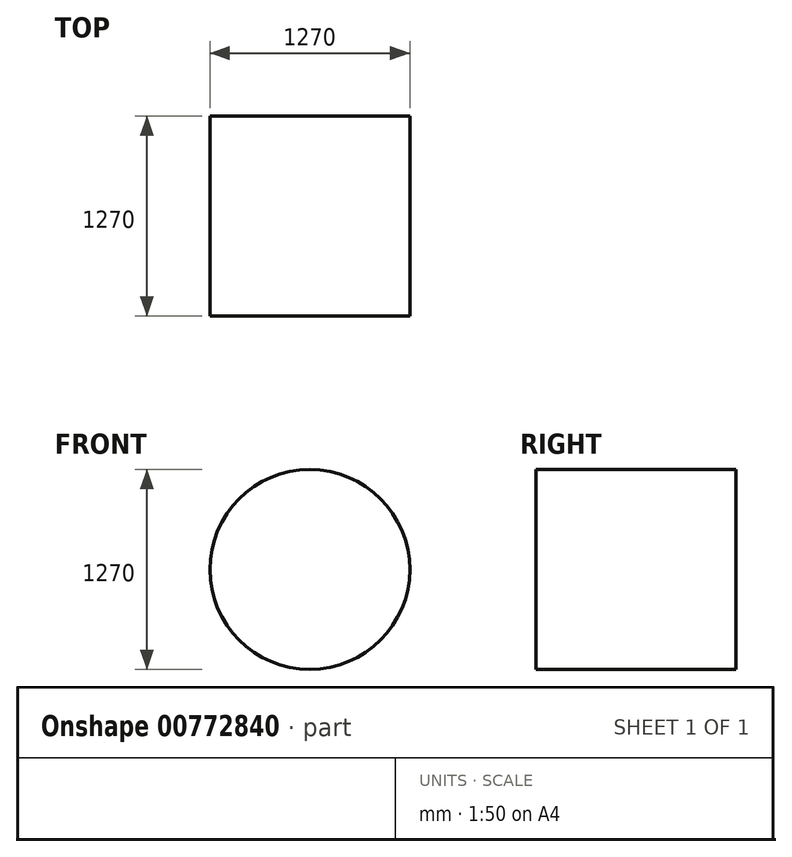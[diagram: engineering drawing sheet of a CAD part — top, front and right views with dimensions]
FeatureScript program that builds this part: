
annotation { "Feature Type Name" : "Feature", "Feature Type Description" : "" }
export const myFeature = defineFeature(function(context is Context, id is Id, definition is map)
    precondition{}
    {
        {
            var Q0;
            Q0=qCreatedBy(makeId("Front.planeOp"),FACE);
            var sketch = newSketch(context, id + "F0", { "sketchPlane" : qUnion([Q0])});
            skCircle(sketch, "E0", {"center": v(-369.55, 338.56) * mm, "radius": 635 * mm});
            skSolve(sketch);
        }
        {
            var Q0;
            Q0=makeQuery(id+"F0.imprint","IMPRINT",FACE,{"disambiguationData":[TD([[makeQuery(id+"F0.imprint","IMPRINT",EDGE,{"derivedFrom":sQuery(id+"F0.wireOp",EDGE,"E0")}),1.0]])]});
            extrude(context, id + "F1", {"entities" : qUnion([Q0]), "depth" : 1270 * mm, "offsetDistance" : 25.4 * mm});
        }
    });
